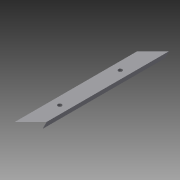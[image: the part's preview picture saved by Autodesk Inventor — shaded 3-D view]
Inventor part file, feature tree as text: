
AUTODESK INVENTOR PART (.ipt)
format: ipt  version: 2015 (Build 190159000, 159)  size: 93,184 bytes
history: native  units: in
note: dims shown in document units (in); Inventor stores cm internally (conversion verified against a paired STEP export)
features: extrude x3, sketch x3, projected_geometry x1
ambient origin geometry x8: Origin, YZ Plane, XZ Plane, XY Plane, X Axis, Y Axis, Z Axis, Center Point
bodies: Solid1 (feature_tree)
feature tree (7):
  extrude  "Extrusion1"  Depth=0.25in
  extrude  "Extrusion2"  Depth=0.25in
  extrude  "Extrusion3"  Depth=0.25in TaperAngle=0.0deg
  sketch  "Sketch1"  dims[d0=1.0in d1=0.25in]
  sketch  "Sketch2"  dims[d2=9.3625in d3=0.0in d6=0.25in]
  projected_geometry  "Projected Loop1"
  sketch  "Sketch3"  dims[d7=0.25in d8=4.8in d9=0.0in d10=3.8in d11=2.075in d12=0.0in]
